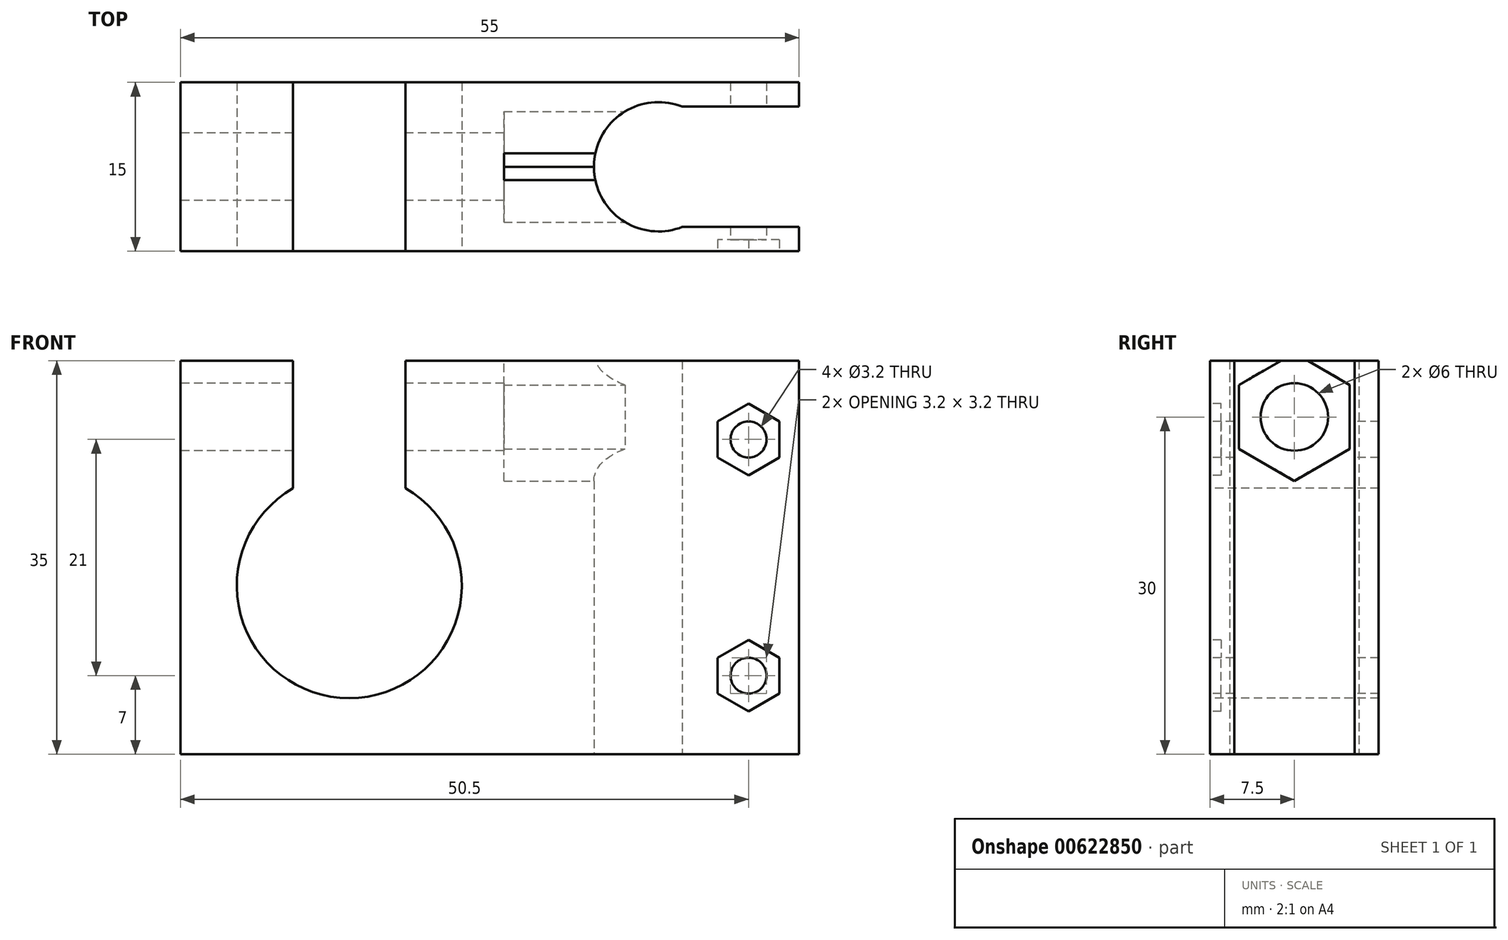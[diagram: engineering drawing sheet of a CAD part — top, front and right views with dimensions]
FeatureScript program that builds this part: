
annotation { "Feature Type Name" : "Feature", "Feature Type Description" : "" }
export const myFeature = defineFeature(function(context is Context, id is Id, definition is map)
    precondition{}
    {
        {
            var Q0;
            Q0=qCreatedBy(makeId("Top.planeOp"),FACE);
            var sketch = newSketch(context, id + "F0", { "sketchPlane" : qUnion([Q0])});
            skLineSegment(sketch, "E0.bottom", {"start": v(27.5, 7.5) * mm, "end": v(-27.5, 7.5) * mm});
            skLineSegment(sketch, "E0.top", {"start": v(27.5, -7.5) * mm, "end": v(-27.5, -7.5) * mm});
            skLineSegment(sketch, "E0.left", {"start": v(27.5, 7.5) * mm, "end": v(27.5, 5.35) * mm});
            skLineSegment(sketch, "E0.right", {"start": v(-27.5, 7.5) * mm, "end": v(-27.5, -7.5) * mm});
            skPoint(sketch, "E0.middle", {"position": v(0, 0) * mm});
            skLineSegment(sketch, "E1", {"start": v(0, 0) * mm, "end": v(27.5, 0) * mm, "construction": true});
            skArc(sketch, "E2", {"start": v(17.1, 5.35) * mm, "mid": v(9.25, 0) * mm, "end": v(17.1, -5.35) * mm});
            skLineSegment(sketch, "E3", {"start": v(17.1, -5.35) * mm, "end": v(27.5, -5.35) * mm});
            skLineSegment(sketch, "E4", {"start": v(17.1, 5.35) * mm, "end": v(27.5, 5.35) * mm});
            skLineSegment(sketch, "E5.trimOffspring", {"start": v(27.5, -5.35) * mm, "end": v(27.5, -7.5) * mm});
            skLineSegment(sketch, "E6", {"start": v(27.5, 5.35) * mm, "end": v(27.5, 0) * mm, "construction": true});
            skLineSegment(sketch, "E7", {"start": v(27.5, -5.35) * mm, "end": v(27.5, 0) * mm, "construction": true});
            skLineSegment(sketch, "E8", {"start": v(9.25, 0) * mm, "end": v(9.25, -7.5) * mm, "construction": true});
            skSolve(sketch);
        }
        {
            var Q0;
            Q0 = qSketchRegion(id + "F0", true);
            extrude(context, id + "F1", {"entities" : qUnion([Q0]), "depth" : 35 * mm, "offsetDistance" : 25 * mm});
        }
        {
            var Q0;
            Q0=makeQuery(id+"F1.opExtrude","SWEPT_FACE",FACE,{"disambiguationData":[OSD([sQuery(id+"F0.wireOp",EDGE,"E0.top")])]});
            var sketch = newSketch(context, id + "F2", { "sketchPlane" : qUnion([Q0])});
            skLineSegment(sketch, "E9", {"start": v(-27.5, 15) * mm, "end": v(27.5, 15) * mm, "construction": true});
            skLineSegment(sketch, "E10.bottom", {"start": v(27.5, 0) * mm, "end": v(23, 0) * mm, "construction": true});
            skLineSegment(sketch, "E10.top", {"start": v(27.5, 7) * mm, "end": v(23, 7) * mm, "construction": true});
            skLineSegment(sketch, "E10.left", {"start": v(27.5, 0) * mm, "end": v(27.5, 7) * mm, "construction": true});
            skLineSegment(sketch, "E10.right", {"start": v(23, 0) * mm, "end": v(23, 7) * mm, "construction": true});
            skLineSegment(sketch, "E11.bottom", {"start": v(27.5, 35) * mm, "end": v(23, 35) * mm, "construction": true});
            skLineSegment(sketch, "E11.top", {"start": v(27.5, 28) * mm, "end": v(23, 28) * mm, "construction": true});
            skLineSegment(sketch, "E11.left", {"start": v(27.5, 35) * mm, "end": v(27.5, 28) * mm, "construction": true});
            skLineSegment(sketch, "E11.right", {"start": v(23, 35) * mm, "end": v(23, 28) * mm, "construction": true});
            skPoint(sketch, "E12", {"position": v(23, 28) * mm});
            skPoint(sketch, "E13", {"position": v(23, 7) * mm});
            skCircle(sketch, "E14", {"center": v(23, 28) * mm, "radius": 3.18 * mm, "construction": true});
            skCircle(sketch, "E15", {"center": v(23, 7) * mm, "radius": 3.18 * mm, "construction": true});
            skLineSegment(sketch, "E16", {"start": v(23, 10.18) * mm, "end": v(25.75, 8.59) * mm});
            skLineSegment(sketch, "E17", {"start": v(25.75, 8.59) * mm, "end": v(25.75, 5.41) * mm});
            skLineSegment(sketch, "E18", {"start": v(25.75, 5.41) * mm, "end": v(23, 3.82) * mm});
            skLineSegment(sketch, "E19", {"start": v(23, 3.82) * mm, "end": v(20.25, 5.41) * mm});
            skLineSegment(sketch, "E20", {"start": v(20.25, 5.41) * mm, "end": v(20.25, 8.59) * mm});
            skLineSegment(sketch, "E21", {"start": v(20.25, 8.59) * mm, "end": v(23, 10.18) * mm});
            skLineSegment(sketch, "E22", {"start": v(23, 31.18) * mm, "end": v(20.25, 29.59) * mm});
            skLineSegment(sketch, "E23", {"start": v(20.25, 29.59) * mm, "end": v(20.25, 26.41) * mm});
            skLineSegment(sketch, "E24", {"start": v(20.25, 26.41) * mm, "end": v(23, 24.82) * mm});
            skLineSegment(sketch, "E25", {"start": v(23, 24.82) * mm, "end": v(25.75, 26.41) * mm});
            skLineSegment(sketch, "E26", {"start": v(25.75, 26.41) * mm, "end": v(25.75, 29.59) * mm});
            skLineSegment(sketch, "E27", {"start": v(25.75, 29.59) * mm, "end": v(23, 31.18) * mm});
            skArc(sketch, "E28", {"start": v(-17.5, 23.66) * mm, "mid": v(-12.5, 5) * mm, "end": v(-7.5, 23.66) * mm});
            skLineSegment(sketch, "E29", {"start": v(-7.5, 35) * mm, "end": v(-7.5, 23.66) * mm});
            skLineSegment(sketch, "E30", {"start": v(-17.5, 23.66) * mm, "end": v(-17.5, 35) * mm});
            skLineSegment(sketch, "E31", {"start": v(-17.5, 25) * mm, "end": v(-7.5, 25) * mm, "construction": true});
            skPoint(sketch, "E32", {"position": v(-12.5, 25) * mm});
            skSolve(sketch);
        }
        {
            var Q0;
            Q0=makeQuery(id+"F2.imprint","IMPRINT",FACE,{"disambiguationData":[TD([[makeQuery(id+"F2.imprint","IMPRINT",EDGE,{"derivedFrom":sQuery(id+"F2.wireOp",EDGE,"E28")}),1.0]])]});
            extrude(context, id + "F3", {"entities" : qUnion([Q0]), "operationType" : NewBodyOperationType.REMOVE, "endBound" : BoundingType.UP_TO_NEXT, "oppositeDirection" : true, "depth" : 25 * mm, "offsetDistance" : 25 * mm});
        }
        {
            var Q0;
            Q0=sQuery(id+"F2.wireOp",VERTEX,"E12");
            var Q1;
            Q1=sQuery(id+"F2.wireOp",VERTEX,"E13");
            var Q2;
            Q2=makeQuery(id+"F1.opExtrude","SWEPT_BODY",BODY,{"disambiguationData":[OSD([sQuery(id+"F0.wireOp",EDGE,"E0.bottom"),sQuery(id+"F0.wireOp",EDGE,"E0.top"),sQuery(id+"F0.wireOp",EDGE,"E0.left"),sQuery(id+"F0.wireOp",EDGE,"E0.right"),sQuery(id+"F0.wireOp",EDGE,"E2"),sQuery(id+"F0.wireOp",EDGE,"E3"),sQuery(id+"F0.wireOp",EDGE,"E4"),sQuery(id+"F0.wireOp",EDGE,"E5.trimOffspring")])]});
            hole(context, id + "F4", {"style" : HoleStyle.SIMPLE, "endStyle" : HoleEndStyle.THROUGH, "holeDiameter" : 3.2 * mm, "majorDiameter" : 5 * mm, "isTappedThrough" : true, "tappedDepth" : 12 * mm, "tapClearance" : 3, "locations" : qUnion([Q0, Q1]), "scope" : qUnion([Q2])});
        }
        {
            var Q0;
            Q0=makeQuery(id+"F2.imprint","IMPRINT",FACE,{"disambiguationData":[TD([[makeQuery(id+"F2.imprint","IMPRINT",EDGE,{"derivedFrom":sQuery(id+"F2.wireOp",EDGE,"E22")}),1.0]])]});
            var Q1;
            Q1=makeQuery(id+"F2.imprint","IMPRINT",FACE,{"disambiguationData":[TD([[makeQuery(id+"F2.imprint","IMPRINT",EDGE,{"derivedFrom":sQuery(id+"F2.wireOp",EDGE,"E16")}),-1.0]])]});
            extrude(context, id + "F5", {"entities" : qUnion([Q0, Q1]), "operationType" : NewBodyOperationType.REMOVE, "oppositeDirection" : true, "depth" : 1 * mm, "offsetDistance" : 25 * mm});
        }
        {
            var Q0;
            Q0=makeQuery(id+"F1.opExtrude","SWEPT_FACE",FACE,{"disambiguationData":[OSD([sQuery(id+"F0.wireOp",EDGE,"E0.right")])]});
            var sketch = newSketch(context, id + "F6", { "sketchPlane" : qUnion([Q0])});
            skCircle(sketch, "E33", {"center": v(0, 30) * mm, "radius": 3 * mm});
            skLineSegment(sketch, "E34.bottom", {"start": v(0, 35) * mm, "end": v(7.5, 35) * mm, "construction": true});
            skLineSegment(sketch, "E34.top", {"start": v(0, 30) * mm, "end": v(7.5, 30) * mm, "construction": true});
            skLineSegment(sketch, "E34.left", {"start": v(0, 35) * mm, "end": v(0, 30) * mm, "construction": true});
            skLineSegment(sketch, "E34.right", {"start": v(7.5, 35) * mm, "end": v(7.5, 30) * mm, "construction": true});
            skSolve(sketch);
        }
        {
            var Q0;
            Q0=makeQuery(id+"F6.imprint","IMPRINT",FACE,{"disambiguationData":[TD([[makeQuery(id+"F6.imprint","IMPRINT",EDGE,{"derivedFrom":sQuery(id+"F6.wireOp",EDGE,"E33")}),1.0]])]});
            extrude(context, id + "F7", {"entities" : qUnion([Q0]), "operationType" : NewBodyOperationType.REMOVE, "endBound" : BoundingType.THROUGH_ALL, "oppositeDirection" : true, "depth" : 25 * mm, "offsetDistance" : 25 * mm});
        }
        {
            var Q0;
            Q0=makeQuery(id+"F1.opExtrude","CAP_EDGE",EDGE,{"disambiguationData":[OSD([sQuery(id+"F0.wireOp",EDGE,"E2")])],"isStart":false});
            cPoint(context, id + "F8", {"entities" : qUnion([Q0]), "parameter" : 0.5});
        }
        {
            var Q0;
            Q0=sQuery(id+"F0.wireOp",EDGE,"E2");
            cPoint(context, id + "F9", {"entities" : qUnion([Q0]), "parameter" : 0.5});
        }
        {
            var Q0;
            Q0 = qCreatedBy(id + "F8" ,VERTEX);
            var Q1;
            Q1=sQuery(id+"F0.wireOp",VERTEX,"E8.end");
            var Q2;
            Q2 = qCreatedBy(id + "F9" ,VERTEX);
            cPlane(context, id + "F10", {"entities" : qUnion([Q0, Q1, Q2]), "cplaneType" : CPlaneType.THREE_POINT, "offset" : 25 * mm, "width" : 150 * mm, "height" : 150 * mm});
        }
        {
            var Q0;
            Q0=qCreatedBy(id+"F10.planeOp",FACE);
            cPlane(context, id + "F11", {"entities" : qUnion([Q0]), "cplaneType" : CPlaneType.OFFSET, "offset" : 3 * mm, "oppositeDirection" : true, "width" : 150 * mm, "height" : 150 * mm});
        }
        {
            var Q0;
            Q0=qCreatedBy(id+"F11.planeOp",FACE);
            var sketch = newSketch(context, id + "F12", { "sketchPlane" : qUnion([Q0])});
            skCircle(sketch, "E35", {"center": v(0, 30) * mm, "radius": 5.69 * mm, "construction": true});
            skLineSegment(sketch, "E36", {"start": v(-4.93, 32.84) * mm, "end": v(-4.93, 27.16) * mm});
            skLineSegment(sketch, "E37", {"start": v(-4.93, 27.16) * mm, "end": v(0, 24.31) * mm});
            skLineSegment(sketch, "E38", {"start": v(0, 24.31) * mm, "end": v(4.92, 27.16) * mm});
            skLineSegment(sketch, "E39", {"start": v(4.92, 27.16) * mm, "end": v(4.92, 32.84) * mm});
            skLineSegment(sketch, "E40", {"start": v(4.92, 32.84) * mm, "end": v(0, 35.69) * mm});
            skLineSegment(sketch, "E41", {"start": v(0, 35.69) * mm, "end": v(-4.93, 32.84) * mm});
            skLineSegment(sketch, "E42", {"start": v(0, 33) * mm, "end": v(0, 27) * mm, "construction": true});
            skSolve(sketch);
        }
        {
            var Q0;
            Q0 = qSketchRegion(id + "F12", true);
            extrude(context, id + "F13", {"entities" : qUnion([Q0]), "operationType" : NewBodyOperationType.REMOVE, "depth" : 11 * mm, "offsetDistance" : 25 * mm});
        }
    });
